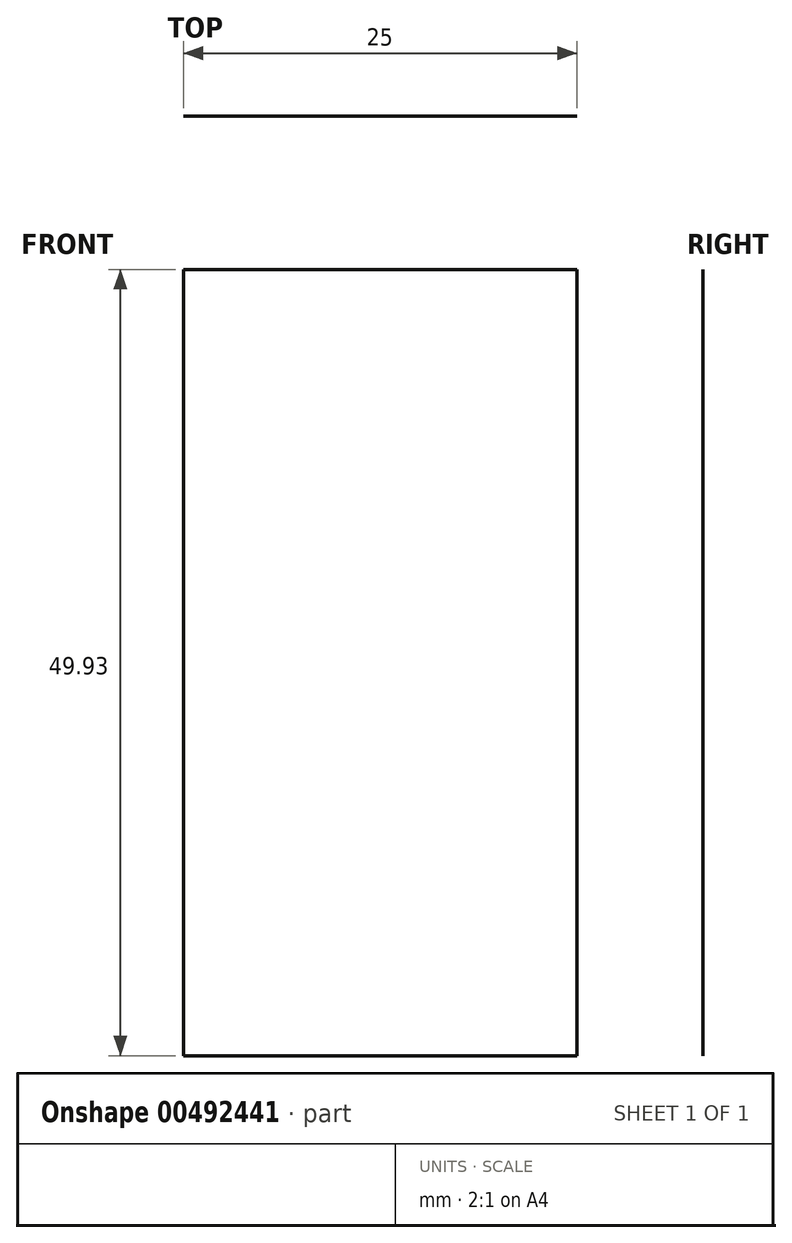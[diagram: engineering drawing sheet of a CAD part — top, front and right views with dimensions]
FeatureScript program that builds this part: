
annotation { "Feature Type Name" : "Feature", "Feature Type Description" : "" }
export const myFeature = defineFeature(function(context is Context, id is Id, definition is map)
    precondition{}
    {
        {
            var Q0;
            Q0=qCreatedBy(makeId("Right.planeOp"),FACE);
            var sketch = newSketch(context, id + "F0", { "sketchPlane" : qUnion([Q0])});
            skFitSpline(sketch, "E0", {"points": [v(-64.89, 41.71) * mm, v(-43.47, 59.2) * mm, v(-3.68, 37.32) * mm, v(34.14, 66.98) * mm, v(53.14, 51.47) * mm, v(76.12, 34.62) * mm, v(-46.34, 25.92) * mm, v(-64.89, 41.71) * mm]});
            skFitSpline(sketch, "E1.0", {"points": [v(-77.26, 41.3) * mm, v(-76.75, 44.39) * mm, v(-75.93, 47.27) * mm, v(-74.5, 50.92) * mm, v(-72.16, 55.19) * mm, v(-68.57, 59.92) * mm, v(-64.92, 63.5) * mm, v(-61.58, 66.04) * mm, v(-58.83, 67.76) * mm, v(-55.84, 69.24) * mm, v(-52.57, 70.42) * mm, v(-49.63, 71.08) * mm, v(-47.16, 71.36) * mm, v(-45.27, 71.44) * mm, v(-43.65, 71.38) * mm, v(-42.35, 71.26) * mm, v(-41.04, 71.08) * mm, v(-39.47, 70.77) * mm, v(-37.67, 70.28) * mm, v(-35.96, 69.7) * mm, v(-33.8, 68.83) * mm, v(-31.31, 67.59) * mm, v(-28.57, 65.94) * mm, v(-26.03, 64.2) * mm, v(-23.63, 62.42) * mm, v(-20.6, 60.03) * mm, v(-17.05, 57.08) * mm, v(-13.8, 54.43) * mm, v(-11.42, 52.65) * mm, v(-9.77, 51.52) * mm, v(-8.3, 50.61) * mm, v(-7.03, 49.96) * mm, v(-6.03, 49.57) * mm, v(-5.46, 49.42) * mm, v(-5.17, 49.37) * mm, v(-5.02, 49.35) * mm, v(-4.95, 49.35) * mm, v(-4.9, 49.36) * mm, v(-4.9, 49.36) * mm, v(-4.86, 49.36) * mm, v(-4.78, 49.38) * mm, v(-4.62, 49.41) * mm, v(-4.33, 49.5) * mm, v(-3.82, 49.7) * mm, v(-2.97, 50.1) * mm, v(-1.67, 50.9) * mm, v(-0.17, 51.98) * mm, v(1.48, 53.33) * mm, v(3.23, 54.9) * mm, v(5.66, 57.23) * mm, v(8.81, 60.5) * mm, v(12.03, 64) * mm, v(14.64, 66.78) * mm, v(16.62, 68.83) * mm, v(18.65, 70.83) * mm, v(20.76, 72.76) * mm, v(22.65, 74.3) * mm, v(24.3, 75.48) * mm, v(25.64, 76.34) * mm, v(27.1, 77.16) * mm, v(28.46, 77.8) * mm, v(29.66, 78.25) * mm, v(30.61, 78.56) * mm, v(31.63, 78.83) * mm, v(32.67, 79.05) * mm, v(33.73, 79.2) * mm, v(35.17, 79.31) * mm, v(36.99, 79.29) * mm, v(39.1, 78.99) * mm, v(41.07, 78.46) * mm, v(42.86, 77.77) * mm, v(44.98, 76.7) * mm, v(47.16, 75.2) * mm, v(49.22, 73.39) * mm, v(50.93, 71.63) * mm, v(52.42, 69.94) * mm, v(53.79, 68.32) * mm, v(55.08, 66.76) * mm, v(56.34, 65.29) * mm, v(57.58, 63.9) * mm, v(58.62, 62.82) * mm, v(59.45, 62.02) * mm, v(59.97, 61.54) * mm, v(60.4, 61.17) * mm, v(60.72, 60.9) * mm, v(61.04, 60.64) * mm, v(61.5, 60.28) * mm, v(62.1, 59.83) * mm, v(63.15, 59.08) * mm, v(64.6, 58.13) * mm, v(66.5, 56.97) * mm, v(68.5, 55.82) * mm, v(70.57, 54.67) * mm, v(72.67, 53.53) * mm, v(74.78, 52.38) * mm, v(76.86, 51.2) * mm, v(78.93, 49.96) * mm, v(80.67, 48.8) * mm, v(82.1, 47.7) * mm, v(83.22, 46.74) * mm, v(84.38, 45.58) * mm, v(85.6, 44.12) * mm, v(86.64, 42.53) * mm, v(87.4, 40.94) * mm, v(87.89, 39.58) * mm, v(88.27, 38.05) * mm, v(88.48, 36.38) * mm, v(88.48, 34.61) * mm, v(88.25, 32.83) * mm, v(87.8, 31.12) * mm, v(87.15, 29.55) * mm, v(86.38, 28.15) * mm, v(85.55, 26.97) * mm, v(84.71, 25.97) * mm, v(83.6, 24.85) * mm, v(82.28, 23.77) * mm, v(80.78, 22.77) * mm, v(79.34, 21.97) * mm, v(77.94, 21.3) * mm, v(76.06, 20.5) * mm, v(73.66, 19.64) * mm, v(70.6, 18.74) * mm, v(67.33, 17.92) * mm, v(63.82, 17.16) * mm, v(60.07, 16.45) * mm, v(56.1, 15.78) * mm, v(51.9, 15.16) * mm, v(46.05, 14.38) * mm, v(38.29, 13.51) * mm, v(28.42, 12.65) * mm, v(18.18, 11.97) * mm, v(7.77, 11.5) * mm, v(-2.65, 11.24) * mm, v(-12.89, 11.22) * mm, v(-22.75, 11.45) * mm, v(-32.09, 11.95) * mm, v(-39.3, 12.63) * mm, v(-44.66, 13.35) * mm, v(-48.48, 13.98) * mm, v(-52.1, 14.73) * mm, v(-56.61, 15.9) * mm, v(-60.76, 17.34) * mm, v(-64.61, 19.2) * mm, v(-67.36, 20.87) * mm, v(-69.95, 22.88) * mm, v(-72.31, 25.27) * mm, v(-74.36, 28.08) * mm, v(-75.94, 31.25) * mm, v(-76.94, 34.62) * mm, v(-77.36, 38.02) * mm, v(-77.26, 41.3) * mm, v(-76.75, 44.39) * mm, v(-75.93, 47.27) * mm, v(-77.26, 41.3) * mm]});
            skLineSegment(sketch, "E2", {"start": v(43.96, -13.91) * mm, "end": v(43.96, -63.84) * mm});
            skLineSegment(sketch, "E3", {"start": v(-70.46, -13.78) * mm, "end": v(-23.47, -8.64) * mm});
            skLineSegment(sketch, "E4", {"start": v(-23.47, -8.64) * mm, "end": v(-14.1, -21.33) * mm});
            skLineSegment(sketch, "E5", {"start": v(-14.1, -21.33) * mm, "end": v(40.9, -12.3) * mm});
            skSolve(sketch);
        }
        {
            var Q0;
            Q0=sQuery(id+"F0.wireOp",EDGE,"E2");
            extrude(context, id + "F1", {"bodyType" : ToolBodyType.SURFACE, "surfaceEntities" : qUnion([Q0]), "depth" : 25 * mm});
        }
        {
            var Q0;
            Q0=qCreatedBy(makeId("Front.planeOp"),FACE);
            var sketch = newSketch(context, id + "F2", { "sketchPlane" : qUnion([Q0])});
            skFitSpline(sketch, "E6", {"points": [v(-48.82, -43.03) * mm, v(-27.18, -33.34) * mm, v(0, -31.63) * mm, v(50.06, -38.88) * mm], "startDerivative": vector(75.86, 60.32) * mm, "endDerivative": vector(119.76, 61.08) * mm});
            skSolve(sketch);
        }
        {
            var Q0;
            Q0=qCreatedBy(makeId("Right.planeOp"),FACE);
            var sketch = newSketch(context, id + "F3", { "sketchPlane" : qUnion([Q0])});
            skFitSpline(sketch, "E7", {"points": [v(24.54, -40.98) * mm, v(0, -31.7) * mm, v(-28.48, -36.47) * mm], "startDerivative": vector(-54.44, 28.89) * mm, "endDerivative": vector(-51.58, -20.47) * mm});
            skSolve(sketch);
        }
    });
